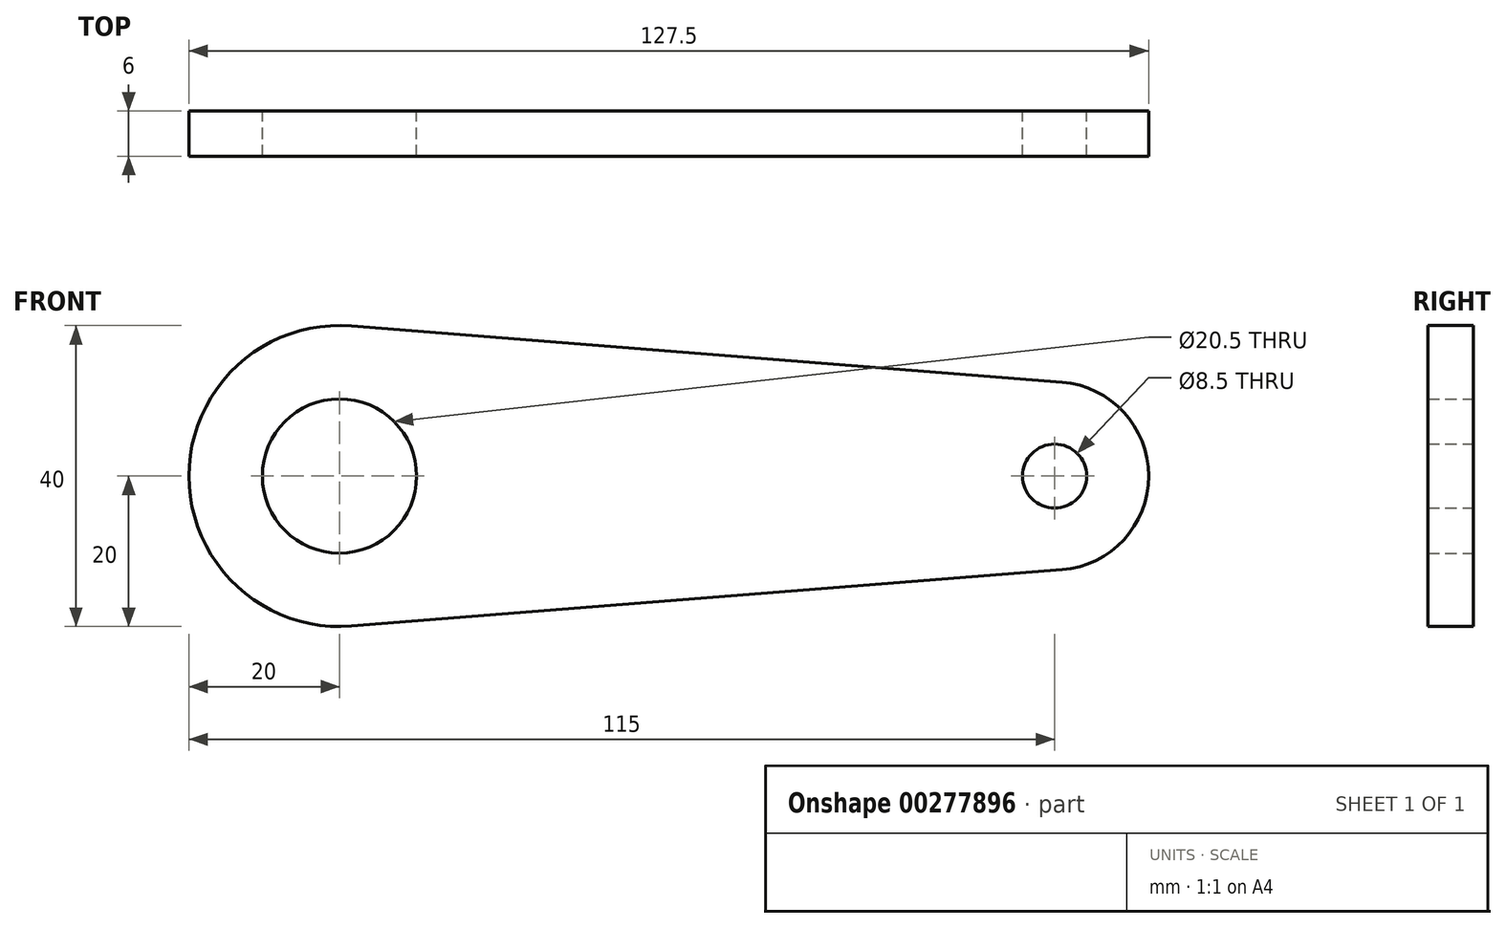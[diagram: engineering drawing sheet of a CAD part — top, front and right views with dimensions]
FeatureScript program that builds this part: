
annotation { "Feature Type Name" : "Feature", "Feature Type Description" : "" }
export const myFeature = defineFeature(function(context is Context, id is Id, definition is map)
    precondition{}
    {
        {
            var Q0;
            Q0=qCreatedBy(makeId("Front.planeOp"),FACE);
            var sketch = newSketch(context, id + "F0", { "sketchPlane" : qUnion([Q0])});
            skArc(sketch, "E0", {"start": v(1.58, 19.94) * mm, "mid": v(-20, 0) * mm, "end": v(1.58, -19.94) * mm});
            skArc(sketch, "E1", {"start": v(95.99, -12.46) * mm, "mid": v(107.5, 0) * mm, "end": v(95.99, 12.46) * mm});
            skLineSegment(sketch, "E2", {"start": v(1.58, 19.94) * mm, "end": v(95.99, 12.46) * mm});
            skLineSegment(sketch, "E3", {"start": v(1.58, -19.94) * mm, "end": v(95.99, -12.46) * mm});
            skCircle(sketch, "E4", {"center": v(0, 0) * mm, "radius": 10.25 * mm});
            skCircle(sketch, "E5", {"center": v(95, 0) * mm, "radius": 4.25 * mm});
            skSolve(sketch);
        }
        {
            var Q0;
            Q0=makeQuery(id+"F0.imprint","IMPRINT",FACE,{"disambiguationData":[TD([[makeQuery(id+"F0.imprint","IMPRINT",EDGE,{"derivedFrom":sQuery(id+"F0.wireOp",EDGE,"E0")}),1.0]])]});
            extrude(context, id + "F1", {"entities" : qUnion([Q0]), "endBound" : BoundingType.SYMMETRIC, "depth" : 6 * mm});
        }
    });
